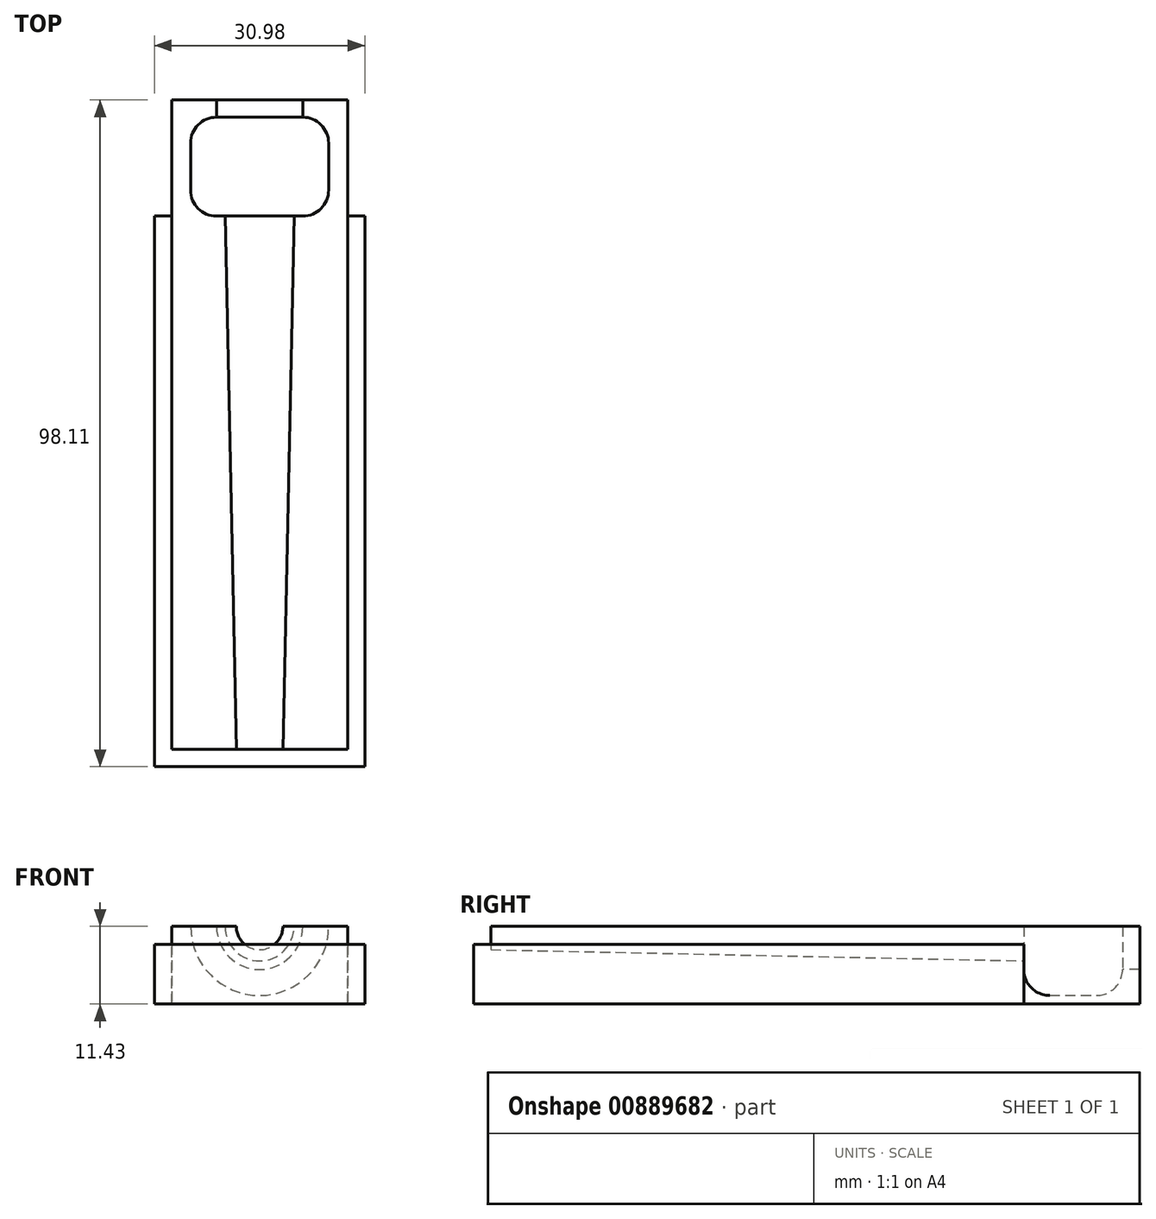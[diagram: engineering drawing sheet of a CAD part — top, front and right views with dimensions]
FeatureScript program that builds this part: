
annotation { "Feature Type Name" : "Feature", "Feature Type Description" : "" }
export const myFeature = defineFeature(function(context is Context, id is Id, definition is map)
    precondition{}
    {
        {
            var Q0;
            Q0=qCreatedBy(makeId("Top.planeOp"),FACE);
            var sketch = newSketch(context, id + "F0", { "sketchPlane" : qUnion([Q0])});
            skLineSegment(sketch, "E0.bottom", {"start": v(12.95, -39.24) * mm, "end": v(-12.95, -39.24) * mm});
            skLineSegment(sketch, "E0.top", {"start": v(12.95, 39.24) * mm, "end": v(-12.95, 39.24) * mm});
            skLineSegment(sketch, "E0.left", {"start": v(12.95, -39.24) * mm, "end": v(12.95, 39.24) * mm});
            skLineSegment(sketch, "E0.right", {"start": v(-12.95, -39.24) * mm, "end": v(-12.95, 39.24) * mm});
            skPoint(sketch, "E0.middle", {"position": v(0, 0) * mm});
            skPoint(sketch, "E1", {"position": v(12.95, 39.24) * mm});
            skPoint(sketch, "E2", {"position": v(-12.95, 39.24) * mm});
            skSolve(sketch);
        }
        {
            var Q0;
            Q0=makeQuery(id+"F0.imprint","IMPRINT",FACE,{"disambiguationData":[TD([[makeQuery(id+"F0.imprint","IMPRINT",EDGE,{"derivedFrom":sQuery(id+"F0.wireOp",EDGE,"E0.bottom")}),-1.0]])]});
            extrude(context, id + "F1", {"entities" : qUnion([Q0]), "oppositeDirection" : true, "depth" : 11.43 * mm, "offsetDistance" : 25.4 * mm});
        }
        {
            var Q0;
            Q0=makeQuery(id+"F1.opExtrude","CAP_FACE",FACE,{"disambiguationData":[OSD([sQuery(id+"F0.wireOp",EDGE,"E0.bottom"),sQuery(id+"F0.wireOp",EDGE,"E0.top"),sQuery(id+"F0.wireOp",EDGE,"E0.left"),sQuery(id+"F0.wireOp",EDGE,"E0.right")])],"isStart":true});
            var sketch = newSketch(context, id + "F2", { "sketchPlane" : qUnion([Q0])});
            skLineSegment(sketch, "E3", {"start": v(0, -39.24) * mm, "end": v(0, 39.24) * mm});
            skLineSegment(sketch, "E4", {"start": v(0, -39.24) * mm, "end": v(3.43, -39.24) * mm});
            skLineSegment(sketch, "E5", {"start": v(0, 39.24) * mm, "end": v(5.08, 39.24) * mm});
            skLineSegment(sketch, "E6", {"start": v(5.08, 39.24) * mm, "end": v(3.43, -39.24) * mm});
            skSolve(sketch);
        }
        {
            var Q0;
            Q0 = qSketchRegion(id + "F2", true);
            var Q1;
            Q1=sQuery(id+"F2.wireOp",EDGE,"E3");
            revolve(context, id + "F3", {"operationType" : NewBodyOperationType.REMOVE, "surfaceOperationType" : NewSurfaceOperationType.NEW, "entities" : qUnion([Q0]), "axis" : qUnion([Q1]), "revolveType" : RevolveType.FULL, "oppositeDirection" : true});
        }
        {
            var Q0;
            Q0=qCreatedBy(makeId("Top.planeOp"),FACE);
            var sketch = newSketch(context, id + "F4", { "sketchPlane" : qUnion([Q0])});
            skLineSegment(sketch, "E7", {"start": v(0, 39.24) * mm, "end": v(-12.95, 39.24) * mm});
            skLineSegment(sketch, "E8", {"start": v(-12.95, 39.24) * mm, "end": v(-12.95, 53.8) * mm});
            skLineSegment(sketch, "E9", {"start": v(-12.95, 53.8) * mm, "end": v(12.95, 53.8) * mm});
            skLineSegment(sketch, "E10", {"start": v(12.95, 53.8) * mm, "end": v(12.95, 39.24) * mm});
            skLineSegment(sketch, "E11", {"start": v(12.95, 39.24) * mm, "end": v(0, 39.24) * mm});
            skSolve(sketch);
        }
        {
            var Q0;
            Q0 = qSketchRegion(id + "F4", true);
            extrude(context, id + "F5", {"entities" : qUnion([Q0]), "oppositeDirection" : true, "depth" : 11.43 * mm, "offsetDistance" : 25.4 * mm});
        }
        {
            var Q0;
            Q0=makeQuery(id+"F5.opExtrude","CAP_FACE",FACE,{"disambiguationData":[OSD([sQuery(id+"F4.wireOp",EDGE,"E7"),sQuery(id+"F4.wireOp",EDGE,"E8"),sQuery(id+"F4.wireOp",EDGE,"E9"),sQuery(id+"F4.wireOp",EDGE,"E10"),sQuery(id+"F4.wireOp",EDGE,"E11")])],"isStart":true});
            var sketch = newSketch(context, id + "F6", { "sketchPlane" : qUnion([Q0])});
            skLineSegment(sketch, "E12", {"start": v(0, 39.24) * mm, "end": v(0, 53.8) * mm});
            skLineSegment(sketch, "E13", {"start": v(0, 53.8) * mm, "end": v(6.35, 53.8) * mm});
            skLineSegment(sketch, "E14", {"start": v(0, 39.24) * mm, "end": v(6.35, 39.24) * mm});
            skLineSegment(sketch, "E15", {"start": v(10.16, 43.05) * mm, "end": v(10.16, 49.98) * mm});
            skPoint(sketch, "E16.visualSharp", {"position": v(10.16, 53.8) * mm});
            skArc(sketch, "E16.filletArc", {"start": v(10.16, 49.98) * mm, "mid": v(9.04, 52.68) * mm, "end": v(6.35, 53.8) * mm});
            skPoint(sketch, "E17.visualSharp", {"position": v(10.16, 39.24) * mm});
            skArc(sketch, "E17.filletArc", {"start": v(6.35, 39.24) * mm, "mid": v(9.04, 40.36) * mm, "end": v(10.16, 43.05) * mm});
            skSolve(sketch);
        }
        {
            var Q0;
            Q0=makeQuery(id+"F6.imprint","IMPRINT",FACE,{"disambiguationData":[TD([[makeQuery(id+"F6.imprint","IMPRINT",EDGE,{"derivedFrom":sQuery(id+"F6.wireOp",EDGE,"E12")}),-1.0]])]});
            var Q1;
            Q1=sQuery(id+"F6.wireOp",EDGE,"E12");
            revolve(context, id + "F7", {"operationType" : NewBodyOperationType.REMOVE, "surfaceOperationType" : NewSurfaceOperationType.NEW, "entities" : qUnion([Q0]), "axis" : qUnion([Q1]), "revolveType" : RevolveType.FULL, "oppositeDirection" : true});
        }
        {
            var Q0;
            Q0=makeQuery(id+"F5.opExtrude","SWEPT_FACE",FACE,{"disambiguationData":[OSD([sQuery(id+"F4.wireOp",EDGE,"E9")])]});
            var sketch = newSketch(context, id + "F8", { "sketchPlane" : qUnion([Q0])});
            skLineSegment(sketch, "E18.bottom", {"start": v(12.95, 0) * mm, "end": v(-12.95, 0) * mm});
            skLineSegment(sketch, "E18.top", {"start": v(12.95, -11.43) * mm, "end": v(-12.95, -11.43) * mm});
            skLineSegment(sketch, "E18.left", {"start": v(12.95, 0) * mm, "end": v(12.95, -11.43) * mm});
            skLineSegment(sketch, "E18.right", {"start": v(-12.95, 0) * mm, "end": v(-12.95, -11.43) * mm});
            skCircle(sketch, "E19", {"center": v(0, 0) * mm, "radius": 3.81 * mm});
            skSolve(sketch);
        }
        {
            var Q0;
            Q0=makeQuery(id+"F8.imprint","IMPRINT",FACE,{"disambiguationData":[TD([[makeQuery(id+"F8.imprint","IMPRINT",EDGE,{"derivedFrom":sQuery(id+"F8.wireOp",EDGE,"E18.top")}),-1.0]])]});
            var Q1;
            {var subQ1=makeQuery(id+"F7.boolean.opBoolean","COPY",EDGE,{"derivedFrom":makeQuery(id+"F7.opRevolve","SWEPT_EDGE",EDGE,{"disambiguationData":[OSD([sQuery(id+"F4.wireOp",EDGE,"E9"),sQuery(id+"F6.wireOp",EDGE,"E13"),sQuery(id+"F6.wireOp",EDGE,"E16.filletArc")])]})});Q1=makeQuery(id+"F8.imprint","IMPRINT",FACE,{"disambiguationData":[TD([[makeQuery(id+"F8.imprint","IMPRINT",EDGE,{"derivedFrom":subQ1}),1.0]])]});}
            extrude(context, id + "F9", {"entities" : qUnion([Q0, Q1]), "operationType" : NewBodyOperationType.ADD, "depth" : 2.54 * mm, "offsetDistance" : 25.4 * mm});
        }
        {
            var Q0;
            Q0=makeQuery(id+"F1.opExtrude","CAP_FACE",FACE,{"disambiguationData":[OSD([sQuery(id+"F0.wireOp",EDGE,"E0.bottom"),sQuery(id+"F0.wireOp",EDGE,"E0.top"),sQuery(id+"F0.wireOp",EDGE,"E0.left"),sQuery(id+"F0.wireOp",EDGE,"E0.right")])],"isStart":false});
            var sketch = newSketch(context, id + "F10", { "sketchPlane" : qUnion([Q0])});
            skPoint(sketch, "E20.middle", {"position": v(0, 0) * mm});
            skLineSegment(sketch, "E21.bottom", {"start": v(12.95, -39.24) * mm, "end": v(-12.95, -39.24) * mm});
            skLineSegment(sketch, "E21.top", {"start": v(12.95, 39.24) * mm, "end": v(-12.95, 39.24) * mm});
            skLineSegment(sketch, "E21.left", {"start": v(12.95, -39.24) * mm, "end": v(12.95, 39.24) * mm});
            skLineSegment(sketch, "E21.right", {"start": v(-12.95, -39.24) * mm, "end": v(-12.95, 39.24) * mm});
            skLineSegment(sketch, "E22", {"start": v(-12.95, -39.24) * mm, "end": v(-15.5, -39.24) * mm});
            skLineSegment(sketch, "E23", {"start": v(-15.5, -39.24) * mm, "end": v(-15.5, 41.78) * mm});
            skLineSegment(sketch, "E24", {"start": v(-15.5, 41.78) * mm, "end": v(15.5, 41.78) * mm});
            skLineSegment(sketch, "E25", {"start": v(15.5, 41.78) * mm, "end": v(15.5, -39.24) * mm});
            skLineSegment(sketch, "E26", {"start": v(15.5, -39.24) * mm, "end": v(12.95, -39.24) * mm});
            skSolve(sketch);
        }
        {
            var Q0;
            Q0=makeQuery(id+"F10.imprint","IMPRINT",FACE,{"disambiguationData":[TD([[makeQuery(id+"F10.imprint","IMPRINT",EDGE,{"derivedFrom":sQuery(id+"F10.wireOp",EDGE,"E21.top")}),-1.0]])]});
            extrude(context, id + "F11", {"entities" : qUnion([Q0]), "operationType" : NewBodyOperationType.ADD, "oppositeDirection" : true, "depth" : 8.76 * mm, "offsetDistance" : 25.4 * mm});
        }
        {
            var Q0;
            Q0=makeQuery(id+"F11.boolean.opBoolean","MERGE",FACE,{"derivedFrom":[makeQuery(id+"F1.opExtrude","CAP_FACE",FACE,{"disambiguationData":[OSD([sQuery(id+"F0.wireOp",EDGE,"E0.bottom"),sQuery(id+"F0.wireOp",EDGE,"E0.top"),sQuery(id+"F0.wireOp",EDGE,"E0.left"),sQuery(id+"F0.wireOp",EDGE,"E0.right")])],"isStart":false}),makeQuery(id+"F11.opExtrude","CAP_FACE",FACE,{"disambiguationData":[OSD([sQuery(id+"F10.wireOp",EDGE,"E21.top"),sQuery(id+"F10.wireOp",EDGE,"E21.left"),sQuery(id+"F10.wireOp",EDGE,"E21.right"),sQuery(id+"F10.wireOp",EDGE,"E22"),sQuery(id+"F10.wireOp",EDGE,"E23"),sQuery(id+"F10.wireOp",EDGE,"E24"),sQuery(id+"F10.wireOp",EDGE,"E25"),sQuery(id+"F10.wireOp",EDGE,"E26")])],"isStart":true})]});
            shell(context, id + "F12", {"entities" : qUnion([Q0]), "thickness" : 2.54 * mm});
        }
    });
